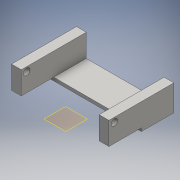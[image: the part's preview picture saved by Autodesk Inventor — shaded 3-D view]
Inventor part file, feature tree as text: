
AUTODESK INVENTOR PART (.ipt)
format: ipt  version: 2016 (Build 200138000, 138)  size: 117,248 bytes
history: native  units: mm
features: extrude x3, sketch x3, other x2
ambient origin geometry x8: Origin, YZ Plane, XZ Plane, XY Plane, X Axis, Y Axis, Z Axis, Center Point
bodies: Body1 (feature_tree)
feature tree (8):
  other  "ソリッド1"
  other  "作業平面1"
  extrude  "押し出し1"  [1 undecoded]
  extrude  "押し出し2"  Depth=90.0mm
  extrude  "押し出し3"  Depth=30.0mm
  sketch  "スケッチ1"
  sketch  "スケッチ2"
  sketch  "スケッチ3"
note: 1 required parameter value undecoded (feature->parameter linkage not recoverable at this tier; creation-order binding heuristic only, values carry confidence <= 0.55)
